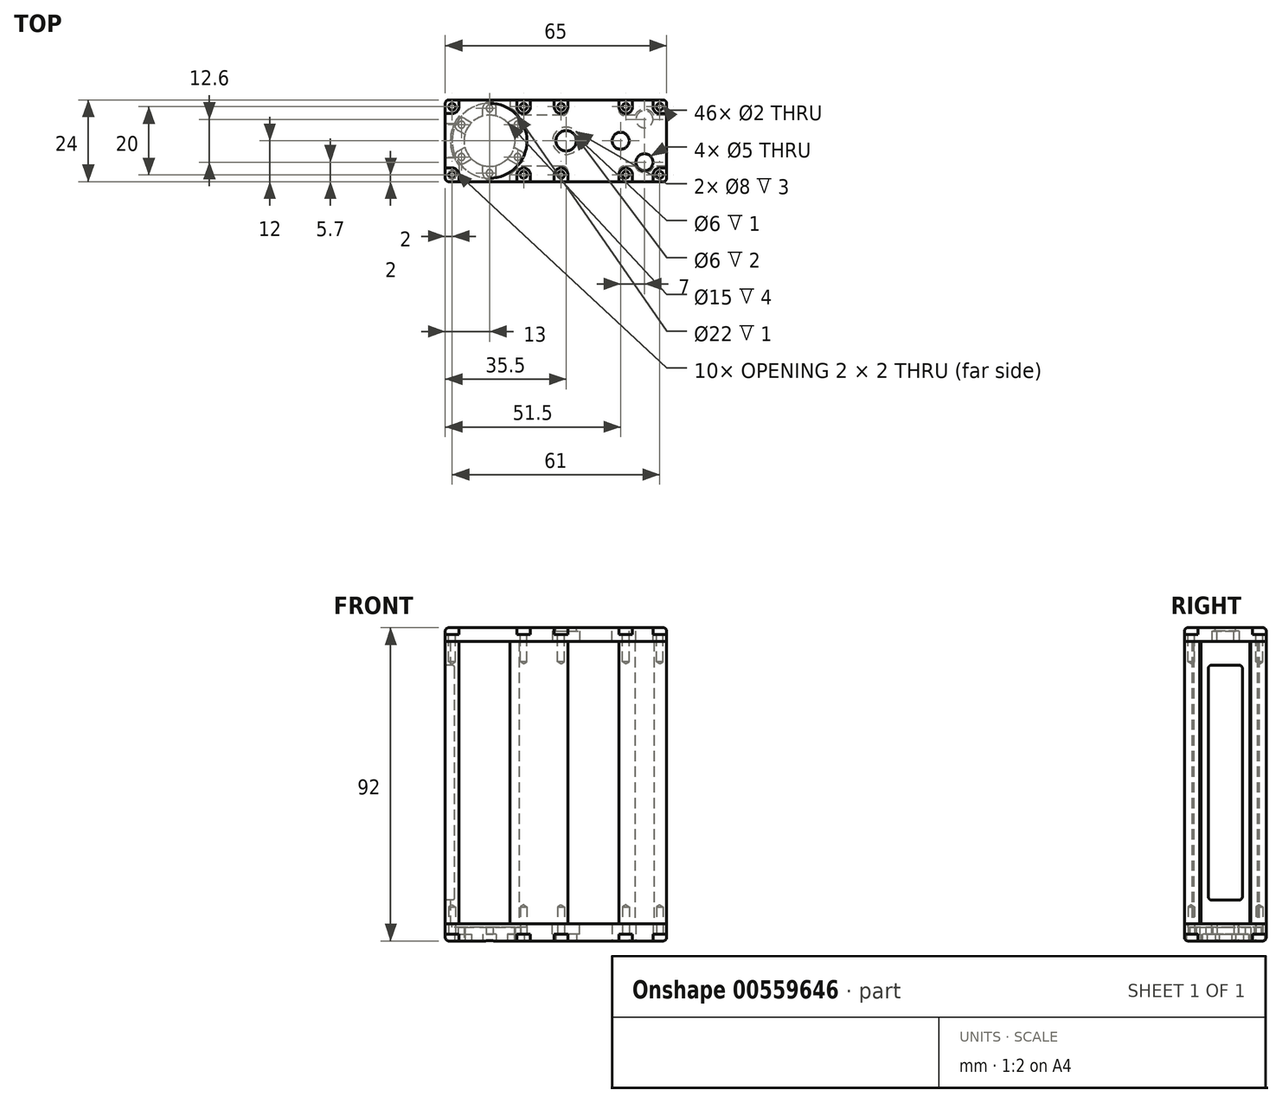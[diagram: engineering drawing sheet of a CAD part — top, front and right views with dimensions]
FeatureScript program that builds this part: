
annotation { "Feature Type Name" : "Feature", "Feature Type Description" : "" }
export const myFeature = defineFeature(function(context is Context, id is Id, definition is map)
    precondition{}
    {
        {
            var Q0;
            Q0=qCreatedBy(makeId("Top.planeOp"),FACE);
            var sketch = newSketch(context, id + "F0", { "sketchPlane" : qUnion([Q0])});
            skLineSegment(sketch, "E0.bottom", {"start": v(0, 0) * mm, "end": v(65, 0) * mm});
            skLineSegment(sketch, "E0.top", {"start": v(0, 24) * mm, "end": v(65, 24) * mm});
            skLineSegment(sketch, "E0.left", {"start": v(0, 0) * mm, "end": v(0, 24) * mm});
            skLineSegment(sketch, "E0.right", {"start": v(65, 0) * mm, "end": v(65, 24) * mm});
            skCircle(sketch, "E1", {"center": v(13, 12) * mm, "radius": 7.5 * mm});
            skCircle(sketch, "E2", {"center": v(35.5, 12) * mm, "radius": 3 * mm});
            skLineSegment(sketch, "E3", {"start": v(0, 12) * mm, "end": v(65, 12) * mm, "construction": true});
            skCircle(sketch, "E4", {"center": v(58.5, 18.3) * mm, "radius": 2.5 * mm});
            skLineSegment(sketch, "E5", {"start": v(58.5, 33.82) * mm, "end": v(58.5, -9.1) * mm, "construction": true});
            skCircle(sketch, "E6", {"center": v(51.5, 12) * mm, "radius": 2.5 * mm});
            skSolve(sketch);
        }
        {
            var Q0;
            Q0=makeQuery(id+"F0.imprint","IMPRINT",FACE,{"disambiguationData":[TD([[makeQuery(id+"F0.imprint","IMPRINT",EDGE,{"derivedFrom":sQuery(id+"F0.wireOp",EDGE,"E0.bottom")}),1.0]])]});
            extrude(context, id + "F1", {"entities" : qUnion([Q0]), "depth" : 5 * mm, "offsetDistance" : 25 * mm});
        }
        {
            var Q0;
            Q0=makeQuery(id+"F1.opExtrude","CAP_FACE",FACE,{"disambiguationData":[OSD([sQuery(id+"F0.wireOp",EDGE,"E0.bottom"),sQuery(id+"F0.wireOp",EDGE,"E0.top"),sQuery(id+"F0.wireOp",EDGE,"E0.left"),sQuery(id+"F0.wireOp",EDGE,"E0.right"),sQuery(id+"F0.wireOp",EDGE,"E1"),sQuery(id+"F0.wireOp",EDGE,"E2"),sQuery(id+"F0.wireOp",EDGE,"IlChBpbm-lz3O-i63i-vyvh-uRPtDYFZDyJ4"),sQuery(id+"F0.wireOp",EDGE,"E4"),sQuery(id+"F0.wireOp",EDGE,"DXnECD94-bbeP-FHQP-F0Iu-yloOuqhtlozA")])],"isStart":false});
            var sketch = newSketch(context, id + "F2", { "sketchPlane" : qUnion([Q0])});
            skCircle(sketch, "E7", {"center": v(13, 12) * mm, "radius": 11 * mm});
            skSolve(sketch);
        }
        {
            var Q0;
            Q0=makeQuery(id+"F2.imprint","IMPRINT",FACE,{"disambiguationData":[TD([[makeQuery(id+"F2.imprint","IMPRINT",EDGE,{"derivedFrom":makeQuery(id+"F1.opExtrude","CAP_EDGE",EDGE,{"disambiguationData":[OSD([sQuery(id+"F0.wireOp",EDGE,"E1")])],"isStart":false})}),-1.0]])]});
            extrude(context, id + "F3", {"entities" : qUnion([Q0]), "operationType" : NewBodyOperationType.REMOVE, "oppositeDirection" : true, "depth" : 1 * mm, "offsetDistance" : 25 * mm});
        }
        {
            var Q0;
            Q0=makeQuery(id+"F1.opExtrude","CAP_FACE",FACE,{"disambiguationData":[OSD([sQuery(id+"F0.wireOp",EDGE,"E0.bottom"),sQuery(id+"F0.wireOp",EDGE,"E0.top"),sQuery(id+"F0.wireOp",EDGE,"E0.left"),sQuery(id+"F0.wireOp",EDGE,"E0.right"),sQuery(id+"F0.wireOp",EDGE,"E1"),sQuery(id+"F0.wireOp",EDGE,"E2"),sQuery(id+"F0.wireOp",EDGE,"IlChBpbm-lz3O-i63i-vyvh-uRPtDYFZDyJ4"),sQuery(id+"F0.wireOp",EDGE,"E4"),sQuery(id+"F0.wireOp",EDGE,"DXnECD94-bbeP-FHQP-F0Iu-yloOuqhtlozA")])],"isStart":true});
            var sketch = newSketch(context, id + "F4", { "sketchPlane" : qUnion([Q0])});
            skCircle(sketch, "E8.cCircle", {"center": v(13, -12) * mm, "radius": 9.5 * mm, "construction": true});
            skLineSegment(sketch, "E8.0", {"start": v(13, -2.5) * mm, "end": v(21.23, -7.25) * mm});
            skLineSegment(sketch, "E8.1", {"start": v(21.23, -7.25) * mm, "end": v(21.23, -16.75) * mm});
            skLineSegment(sketch, "E8.2", {"start": v(21.23, -16.75) * mm, "end": v(13, -21.5) * mm});
            skLineSegment(sketch, "E8.3", {"start": v(13, -21.5) * mm, "end": v(4.77, -16.75) * mm});
            skLineSegment(sketch, "E8.4", {"start": v(4.77, -16.75) * mm, "end": v(4.77, -7.25) * mm});
            skLineSegment(sketch, "E8.5", {"start": v(4.77, -7.25) * mm, "end": v(13, -2.5) * mm});
            skLineSegment(sketch, "E9", {"start": v(13, -2.5) * mm, "end": v(13, -21.5) * mm, "construction": true});
            skPoint(sketch, "E10", {"position": v(13, -2.5) * mm});
            skPoint(sketch, "E11", {"position": v(4.77, -7.25) * mm});
            skPoint(sketch, "E12", {"position": v(4.77, -16.75) * mm});
            skPoint(sketch, "E13", {"position": v(13, -21.5) * mm});
            skPoint(sketch, "E14", {"position": v(21.23, -16.75) * mm});
            skPoint(sketch, "E15", {"position": v(21.23, -7.25) * mm});
            skSolve(sketch);
        }
        {
            var Q0;
            Q0=sQuery(id+"F4.wireOp",VERTEX,"E10");
            var Q1;
            Q1=sQuery(id+"F4.wireOp",VERTEX,"E11");
            var Q2;
            Q2=sQuery(id+"F4.wireOp",VERTEX,"E12");
            var Q3;
            Q3=sQuery(id+"F4.wireOp",VERTEX,"E13");
            var Q4;
            Q4=sQuery(id+"F4.wireOp",VERTEX,"E14");
            var Q5;
            Q5=sQuery(id+"F4.wireOp",VERTEX,"E15");
            var Q6;
            Q6=makeQuery(id+"F1.opExtrude","SWEPT_BODY",BODY,{"disambiguationData":[OSD([sQuery(id+"F0.wireOp",EDGE,"E0.bottom"),sQuery(id+"F0.wireOp",EDGE,"E0.top"),sQuery(id+"F0.wireOp",EDGE,"E0.left"),sQuery(id+"F0.wireOp",EDGE,"E0.right"),sQuery(id+"F0.wireOp",EDGE,"E1"),sQuery(id+"F0.wireOp",EDGE,"E2"),sQuery(id+"F0.wireOp",EDGE,"IlChBpbm-lz3O-i63i-vyvh-uRPtDYFZDyJ4"),sQuery(id+"F0.wireOp",EDGE,"E4"),sQuery(id+"F0.wireOp",EDGE,"DXnECD94-bbeP-FHQP-F0Iu-yloOuqhtlozA")])]});
            hole(context, id + "F5", {"style" : HoleStyle.SIMPLE, "endStyle" : HoleEndStyle.THROUGH, "holeDiameter" : 2 * mm, "isTappedThrough" : true, "tappedDepth" : 5 * mm, "tapClearance" : 2, "startFromSketch" : true, "locations" : qUnion([Q0, Q1, Q2, Q3, Q4, Q5]), "scope" : qUnion([Q6])});
        }
        {
            var Q0;
            Q0=makeQuery(id+"F1.opExtrude","CAP_FACE",FACE,{"disambiguationData":[OSD([sQuery(id+"F0.wireOp",EDGE,"E0.bottom"),sQuery(id+"F0.wireOp",EDGE,"E0.top"),sQuery(id+"F0.wireOp",EDGE,"E0.left"),sQuery(id+"F0.wireOp",EDGE,"E0.right"),sQuery(id+"F0.wireOp",EDGE,"E1"),sQuery(id+"F0.wireOp",EDGE,"E2"),sQuery(id+"F0.wireOp",EDGE,"IlChBpbm-lz3O-i63i-vyvh-uRPtDYFZDyJ4"),sQuery(id+"F0.wireOp",EDGE,"E4"),sQuery(id+"F0.wireOp",EDGE,"DXnECD94-bbeP-FHQP-F0Iu-yloOuqhtlozA")])],"isStart":true});
            var sketch = newSketch(context, id + "F6", { "sketchPlane" : qUnion([Q0])});
            skArc(sketch, "E16", {"start": v(15, -2.5) * mm, "mid": v(13, -0.5) * mm, "end": v(11, -2.5) * mm});
            skArc(sketch, "E17", {"start": v(5.77, -5.52) * mm, "mid": v(3.04, -6.25) * mm, "end": v(3.77, -8.98) * mm});
            skArc(sketch, "E18", {"start": v(3.77, -15.02) * mm, "mid": v(3.04, -17.75) * mm, "end": v(5.77, -18.48) * mm});
            skArc(sketch, "E19", {"start": v(11, -21.5) * mm, "mid": v(13, -23.5) * mm, "end": v(15, -21.5) * mm});
            skArc(sketch, "E20", {"start": v(22.23, -8.98) * mm, "mid": v(22.96, -6.25) * mm, "end": v(20.23, -5.52) * mm});
            skArc(sketch, "E21", {"start": v(20.23, -18.48) * mm, "mid": v(22.96, -17.75) * mm, "end": v(22.23, -15.02) * mm});
            skLineSegment(sketch, "E22", {"start": v(3.77, -8.98) * mm, "end": v(20.23, -18.48) * mm});
            skLineSegment(sketch, "E23", {"start": v(5.77, -5.52) * mm, "end": v(22.23, -15.02) * mm});
            skLineSegment(sketch, "E24", {"start": v(11, -2.5) * mm, "end": v(11, -21.5) * mm});
            skLineSegment(sketch, "E25", {"start": v(15, -2.5) * mm, "end": v(15, -21.5) * mm});
            skLineSegment(sketch, "E26", {"start": v(3.77, -15.02) * mm, "end": v(20.23, -5.52) * mm});
            skLineSegment(sketch, "E27", {"start": v(5.77, -18.48) * mm, "end": v(22.23, -8.98) * mm});
            skSolve(sketch);
        }
        {
            var Q0;
            Q0 = qSketchRegion(id + "F6", true);
            extrude(context, id + "F7", {"entities" : qUnion([Q0]), "operationType" : NewBodyOperationType.REMOVE, "oppositeDirection" : true, "depth" : 2 * mm, "offsetDistance" : 25 * mm});
        }
        {
            var Q0;
            Q0=makeQuery(id+"F1.opExtrude","CAP_FACE",FACE,{"disambiguationData":[OSD([sQuery(id+"F0.wireOp",EDGE,"E0.bottom"),sQuery(id+"F0.wireOp",EDGE,"E0.top"),sQuery(id+"F0.wireOp",EDGE,"E0.left"),sQuery(id+"F0.wireOp",EDGE,"E0.right"),sQuery(id+"F0.wireOp",EDGE,"E1"),sQuery(id+"F0.wireOp",EDGE,"E2"),sQuery(id+"F0.wireOp",EDGE,"E4"),sQuery(id+"F0.wireOp",EDGE,"DXnECD94-bbeP-FHQP-F0Iu-yloOuqhtlozA")])],"isStart":false});
            var sketch = newSketch(context, id + "F8", { "sketchPlane" : qUnion([Q0])});
            skCircle(sketch, "E28", {"center": v(35.5, 12) * mm, "radius": 4 * mm});
            skSolve(sketch);
        }
        {
            var Q0;
            Q0 = qSketchRegion(id + "F8", true);
            extrude(context, id + "F9", {"entities" : qUnion([Q0]), "operationType" : NewBodyOperationType.REMOVE, "oppositeDirection" : true, "depth" : 3 * mm, "offsetDistance" : 25 * mm});
        }
        {
            var Q0;
            Q0=qCreatedBy(makeId("Top.planeOp"),FACE);
            cPlane(context, id + "F10", {"entities" : qUnion([Q0]), "cplaneType" : CPlaneType.OFFSET, "offset" : 92 * mm, "width" : 150 * mm, "height" : 150 * mm});
        }
        {
            var Q0;
            Q0=qCreatedBy(id+"F10.planeOp",FACE);
            var sketch = newSketch(context, id + "F11", { "sketchPlane" : qUnion([Q0])});
            skLineSegment(sketch, "E29.bottom", {"start": v(0, 0) * mm, "end": v(65, 0) * mm});
            skLineSegment(sketch, "E29.top", {"start": v(0, 24) * mm, "end": v(65, 24) * mm});
            skLineSegment(sketch, "E29.left", {"start": v(0, 0) * mm, "end": v(0, 24) * mm});
            skLineSegment(sketch, "E29.right", {"start": v(65, 0) * mm, "end": v(65, 24) * mm});
            skCircle(sketch, "E30", {"center": v(51.5, 12) * mm, "radius": 2.5 * mm});
            skCircle(sketch, "E31", {"center": v(58.5, 5.7) * mm, "radius": 2.5 * mm});
            skCircle(sketch, "E32", {"center": v(35.5, 12) * mm, "radius": 3 * mm});
            skLineSegment(sketch, "E33", {"start": v(0, 12) * mm, "end": v(65, 12) * mm, "construction": true});
            skSolve(sketch);
        }
        {
            var Q0;
            Q0 = qSketchRegion(id + "F11", true);
            extrude(context, id + "F12", {"entities" : qUnion([Q0]), "oppositeDirection" : true, "depth" : 4 * mm, "offsetDistance" : 25 * mm});
        }
        {
            var Q0;
            Q0=makeQuery(id+"F12.opExtrude","CAP_FACE",FACE,{"disambiguationData":[OSD([sQuery(id+"F11.wireOp",EDGE,"E29.bottom"),sQuery(id+"F11.wireOp",EDGE,"E29.top"),sQuery(id+"F11.wireOp",EDGE,"E29.left"),sQuery(id+"F11.wireOp",EDGE,"E29.right"),sQuery(id+"F11.wireOp",EDGE,"E30"),sQuery(id+"F11.wireOp",EDGE,"E31"),sQuery(id+"F11.wireOp",EDGE,"E32")])],"isStart":false});
            var sketch = newSketch(context, id + "F13", { "sketchPlane" : qUnion([Q0])});
            skCircle(sketch, "E34", {"center": v(35.5, -12) * mm, "radius": 4 * mm});
            skSolve(sketch);
        }
        {
            var Q0;
            Q0 = qSketchRegion(id + "F13", true);
            extrude(context, id + "F14", {"entities" : qUnion([Q0]), "operationType" : NewBodyOperationType.REMOVE, "oppositeDirection" : true, "depth" : 3 * mm, "offsetDistance" : 25 * mm});
        }
        {
            var Q0;
            Q0=makeQuery(id+"F1.opExtrude","CAP_FACE",FACE,{"disambiguationData":[OSD([sQuery(id+"F0.wireOp",EDGE,"E0.bottom"),sQuery(id+"F0.wireOp",EDGE,"E0.top"),sQuery(id+"F0.wireOp",EDGE,"E0.left"),sQuery(id+"F0.wireOp",EDGE,"E0.right"),sQuery(id+"F0.wireOp",EDGE,"E1"),sQuery(id+"F0.wireOp",EDGE,"E2"),sQuery(id+"F0.wireOp",EDGE,"E4"),sQuery(id+"F0.wireOp",EDGE,"E6")])],"isStart":false});
            var sketch = newSketch(context, id + "F15", { "sketchPlane" : qUnion([Q0])});
            skLineSegment(sketch, "E35.bottom", {"start": v(0, 24) * mm, "end": v(4, 24) * mm});
            skLineSegment(sketch, "E35.top", {"start": v(0, 0) * mm, "end": v(4, 0) * mm});
            skLineSegment(sketch, "E35.left", {"start": v(0, 24) * mm, "end": v(0, 0) * mm});
            skLineSegment(sketch, "E35.right", {"start": v(4, 24) * mm, "end": v(4, 19.16) * mm});
            skArc(sketch, "E36", {"start": v(4, 19.16) * mm, "mid": v(1.5, 12) * mm, "end": v(4, 4.84) * mm});
            skLineSegment(sketch, "E37.trimOffspring", {"start": v(4, 4.84) * mm, "end": v(4, 0) * mm});
            skLineSegment(sketch, "E38", {"start": v(58.5, 18.3) * mm, "end": v(58.5, 5.7) * mm, "construction": true});
            skArc(sketch, "E39", {"start": v(61.25, 19.5) * mm, "mid": v(58.5, 21.3) * mm, "end": v(55.75, 19.5) * mm});
            skArc(sketch, "E40", {"start": v(55.75, 4.5) * mm, "mid": v(58.5, 2.7) * mm, "end": v(61.25, 4.5) * mm});
            skLineSegment(sketch, "E41.bottom", {"start": v(65, 24) * mm, "end": v(51, 24) * mm});
            skLineSegment(sketch, "E41.top", {"start": v(65, 19.5) * mm, "end": v(61.25, 19.5) * mm});
            skLineSegment(sketch, "E41.left", {"start": v(65, 24) * mm, "end": v(65, 19.5) * mm});
            skLineSegment(sketch, "E41.right", {"start": v(51, 24) * mm, "end": v(51, 21) * mm});
            skLineSegment(sketch, "E42.bottom", {"start": v(65, 0) * mm, "end": v(51, 0) * mm});
            skLineSegment(sketch, "E42.top", {"start": v(65, 4.5) * mm, "end": v(61.25, 4.5) * mm});
            skLineSegment(sketch, "E42.left", {"start": v(65, 0) * mm, "end": v(65, 4.5) * mm});
            skLineSegment(sketch, "E42.right", {"start": v(51, 0) * mm, "end": v(51, 3) * mm});
            skLineSegment(sketch, "E43.trimOffspring", {"start": v(55.75, 19.5) * mm, "end": v(52.5, 19.5) * mm});
            skLineSegment(sketch, "E44.trimOffspring", {"start": v(55.75, 4.5) * mm, "end": v(52.5, 4.5) * mm});
            skArc(sketch, "E45", {"start": v(51, 21) * mm, "mid": v(51.44, 19.94) * mm, "end": v(52.5, 19.5) * mm});
            skArc(sketch, "E46", {"start": v(52.5, 4.5) * mm, "mid": v(51.44, 4.06) * mm, "end": v(51, 3) * mm});
            skPoint(sketch, "E47.orphan", {"position": v(51, 19.5) * mm});
            skPoint(sketch, "E48.orphan", {"position": v(51, 4.5) * mm});
            skLineSegment(sketch, "E49.bottom", {"start": v(36, 24) * mm, "end": v(19, 24) * mm});
            skLineSegment(sketch, "E49.top", {"start": v(34.5, 19.5) * mm, "end": v(21.72, 19.5) * mm});
            skLineSegment(sketch, "E49.left", {"start": v(36, 24) * mm, "end": v(36, 21) * mm});
            skLineSegment(sketch, "E49.right", {"start": v(19, 24) * mm, "end": v(19, 21.81) * mm});
            skLineSegment(sketch, "E50.bottom", {"start": v(36, 0) * mm, "end": v(19, 0) * mm});
            skLineSegment(sketch, "E50.top", {"start": v(34.5, 4.5) * mm, "end": v(21.72, 4.5) * mm});
            skLineSegment(sketch, "E50.left", {"start": v(36, 0) * mm, "end": v(36, 3) * mm});
            skLineSegment(sketch, "E50.right", {"start": v(19, 0) * mm, "end": v(19, 2.19) * mm});
            skLineSegment(sketch, "E51", {"start": v(36, 19.5) * mm, "end": v(36, 4.5) * mm, "construction": true});
            skLineSegment(sketch, "E52", {"start": v(19, 19.5) * mm, "end": v(19, 4.5) * mm, "construction": true});
            skArc(sketch, "E53", {"start": v(34.5, 19.5) * mm, "mid": v(35.56, 19.94) * mm, "end": v(36, 21) * mm});
            skArc(sketch, "E54", {"start": v(36, 3) * mm, "mid": v(35.56, 4.06) * mm, "end": v(34.5, 4.5) * mm});
            skArc(sketch, "E55", {"start": v(21.72, 19.5) * mm, "mid": v(20.45, 20.76) * mm, "end": v(19, 21.81) * mm});
            skArc(sketch, "E56.trimOffspring", {"start": v(19, 2.19) * mm, "mid": v(20.45, 3.24) * mm, "end": v(21.72, 4.5) * mm});
            skSolve(sketch);
        }
        {
            var Q0;
            Q0 = qSketchRegion(id + "F15", true);
            extrude(context, id + "F16", {"entities" : qUnion([Q0]), "depth" : 83 * mm, "offsetDistance" : 25 * mm});
        }
        {
            var Q0;
            Q0=makeQuery(id+"F1.opExtrude","CAP_FACE",FACE,{"disambiguationData":[OSD([sQuery(id+"F0.wireOp",EDGE,"E0.bottom"),sQuery(id+"F0.wireOp",EDGE,"E0.top"),sQuery(id+"F0.wireOp",EDGE,"E0.left"),sQuery(id+"F0.wireOp",EDGE,"E0.right"),sQuery(id+"F0.wireOp",EDGE,"E1"),sQuery(id+"F0.wireOp",EDGE,"E2"),sQuery(id+"F0.wireOp",EDGE,"E4"),sQuery(id+"F0.wireOp",EDGE,"E6")])],"isStart":true});
            var sketch = newSketch(context, id + "F17", { "sketchPlane" : qUnion([Q0])});
            skLineSegment(sketch, "E57.bottom", {"start": v(2, -2) * mm, "end": v(63, -2) * mm, "construction": true});
            skLineSegment(sketch, "E57.top", {"start": v(2, -22) * mm, "end": v(63, -22) * mm, "construction": true});
            skLineSegment(sketch, "E57.left", {"start": v(2, -2) * mm, "end": v(2, -22) * mm, "construction": true});
            skLineSegment(sketch, "E57.right", {"start": v(63, -2) * mm, "end": v(63, -22) * mm, "construction": true});
            skPoint(sketch, "E58", {"position": v(2, -2) * mm});
            skPoint(sketch, "E59", {"position": v(2, -22) * mm});
            skPoint(sketch, "E60", {"position": v(63, -22) * mm});
            skPoint(sketch, "E61", {"position": v(63, -2) * mm});
            skLineSegment(sketch, "E62", {"start": v(53, -2) * mm, "end": v(53, -22) * mm, "construction": true});
            skLineSegment(sketch, "E63", {"start": v(34, -2) * mm, "end": v(34, -22) * mm, "construction": true});
            skLineSegment(sketch, "E64", {"start": v(23, -2) * mm, "end": v(23, -22) * mm, "construction": true});
            skPoint(sketch, "E65", {"position": v(23, -2) * mm});
            skPoint(sketch, "E66", {"position": v(34, -2) * mm});
            skPoint(sketch, "E67", {"position": v(34, -22) * mm});
            skPoint(sketch, "E68", {"position": v(23, -22) * mm});
            skPoint(sketch, "E69", {"position": v(53, -22) * mm});
            skPoint(sketch, "E70", {"position": v(53, -2) * mm});
            skSolve(sketch);
        }
        {
            var Q0;
            Q0=sQuery(id+"F17.wireOp",VERTEX,"E61");
            var Q1;
            Q1=sQuery(id+"F17.wireOp",VERTEX,"E60");
            var Q2;
            Q2=sQuery(id+"F17.wireOp",VERTEX,"E59");
            var Q3;
            Q3=sQuery(id+"F17.wireOp",VERTEX,"E58");
            var Q4;
            Q4=sQuery(id+"F17.wireOp",VERTEX,"E65");
            var Q5;
            Q5=sQuery(id+"F17.wireOp",VERTEX,"E66");
            var Q6;
            Q6=sQuery(id+"F17.wireOp",VERTEX,"E70");
            var Q7;
            Q7=sQuery(id+"F17.wireOp",VERTEX,"E69");
            var Q8;
            Q8=sQuery(id+"F17.wireOp",VERTEX,"E67");
            var Q9;
            Q9=sQuery(id+"F17.wireOp",VERTEX,"E68");
            var Q10;
            Q10=makeQuery(id+"F1.opExtrude","SWEPT_BODY",BODY,{"disambiguationData":[OSD([sQuery(id+"F0.wireOp",EDGE,"E0.bottom"),sQuery(id+"F0.wireOp",EDGE,"E0.top"),sQuery(id+"F0.wireOp",EDGE,"E0.left"),sQuery(id+"F0.wireOp",EDGE,"E0.right"),sQuery(id+"F0.wireOp",EDGE,"E1"),sQuery(id+"F0.wireOp",EDGE,"E2"),sQuery(id+"F0.wireOp",EDGE,"E4"),sQuery(id+"F0.wireOp",EDGE,"E6")])]});
            var Q11;
            Q11=makeQuery(id+"F16.opExtrude","SWEPT_BODY",BODY,{"disambiguationData":[OSD([sQuery(id+"F15.wireOp",EDGE,"sETA7IfB-NbWZ-x8hc-ehO1-osH0QOvT683d.bottom"),sQuery(id+"F15.wireOp",EDGE,"sETA7IfB-NbWZ-x8hc-ehO1-osH0QOvT683d.top"),sQuery(id+"F15.wireOp",EDGE,"sETA7IfB-NbWZ-x8hc-ehO1-osH0QOvT683d.left"),sQuery(id+"F15.wireOp",EDGE,"sETA7IfB-NbWZ-x8hc-ehO1-osH0QOvT683d.right"),sQuery(id+"F15.wireOp",EDGE,"ILhqpvC7-i7Yn-IUXK-iJsS-K77EfisCqqC3.top"),sQuery(id+"F15.wireOp",EDGE,"ILhqpvC7-i7Yn-IUXK-iJsS-K77EfisCqqC3.right"),sQuery(id+"F15.wireOp",EDGE,"2abb0f86-2ee3-4902-80a2-e3a9647c8841.trimOffspring"),sQuery(id+"F15.wireOp",EDGE,"rQa9nioj-B1Bx-91pH-sico-VFbbgBudFIM0")])]});
            var Q12;
            Q12=makeQuery(id+"F16.opExtrude","SWEPT_BODY",BODY,{"disambiguationData":[OSD([sQuery(id+"F15.wireOp",EDGE,"E35.bottom"),sQuery(id+"F15.wireOp",EDGE,"E35.top"),sQuery(id+"F15.wireOp",EDGE,"E35.left"),sQuery(id+"F15.wireOp",EDGE,"E35.right"),sQuery(id+"F15.wireOp",EDGE,"E36"),sQuery(id+"F15.wireOp",EDGE,"E37.trimOffspring")])]});
            var Q13;
            Q13=makeQuery(id+"F16.opExtrude","SWEPT_BODY",BODY,{"disambiguationData":[OSD([sQuery(id+"F15.wireOp",EDGE,"E49.bottom"),sQuery(id+"F15.wireOp",EDGE,"E49.top"),sQuery(id+"F15.wireOp",EDGE,"E49.left"),sQuery(id+"F15.wireOp",EDGE,"E49.right"),sQuery(id+"F15.wireOp",EDGE,"E53"),sQuery(id+"F15.wireOp",EDGE,"E55")])]});
            var Q14;
            Q14=makeQuery(id+"F16.opExtrude","SWEPT_BODY",BODY,{"disambiguationData":[OSD([sQuery(id+"F15.wireOp",EDGE,"E39"),sQuery(id+"F15.wireOp",EDGE,"E41.bottom"),sQuery(id+"F15.wireOp",EDGE,"E41.top"),sQuery(id+"F15.wireOp",EDGE,"E41.left"),sQuery(id+"F15.wireOp",EDGE,"E41.right"),sQuery(id+"F15.wireOp",EDGE,"E43.trimOffspring"),sQuery(id+"F15.wireOp",EDGE,"E45")])]});
            var Q15;
            Q15=makeQuery(id+"F16.opExtrude","SWEPT_BODY",BODY,{"disambiguationData":[OSD([sQuery(id+"F15.wireOp",EDGE,"E40"),sQuery(id+"F15.wireOp",EDGE,"E42.bottom"),sQuery(id+"F15.wireOp",EDGE,"E42.top"),sQuery(id+"F15.wireOp",EDGE,"E42.left"),sQuery(id+"F15.wireOp",EDGE,"E42.right"),sQuery(id+"F15.wireOp",EDGE,"E44.trimOffspring"),sQuery(id+"F15.wireOp",EDGE,"E46")])]});
            var Q16;
            Q16=makeQuery(id+"F16.opExtrude","SWEPT_BODY",BODY,{"disambiguationData":[OSD([sQuery(id+"F15.wireOp",EDGE,"E50.bottom"),sQuery(id+"F15.wireOp",EDGE,"E50.top"),sQuery(id+"F15.wireOp",EDGE,"E50.left"),sQuery(id+"F15.wireOp",EDGE,"E50.right"),sQuery(id+"F15.wireOp",EDGE,"E54"),sQuery(id+"F15.wireOp",EDGE,"E56.trimOffspring")])]});
            hole(context, id + "F18", {"style" : HoleStyle.SIMPLE, "endStyle" : HoleEndStyle.BLIND, "holeDiameter" : 2 * mm, "holeDepth" : 10 * mm, "isTappedThrough" : true, "tappedDepth" : 7 * mm, "tapClearance" : 2, "startFromSketch" : true, "locations" : qUnion([Q0, Q1, Q2, Q3, Q4, Q5, Q6, Q7, Q8, Q9]), "scope" : qUnion([Q10, Q11, Q12, Q13, Q14, Q15, Q16])});
        }
        {
            var Q0;
            Q0=makeQuery(id+"F1.opExtrude","CAP_FACE",FACE,{"disambiguationData":[OSD([sQuery(id+"F0.wireOp",EDGE,"E0.bottom"),sQuery(id+"F0.wireOp",EDGE,"E0.top"),sQuery(id+"F0.wireOp",EDGE,"E0.left"),sQuery(id+"F0.wireOp",EDGE,"E0.right"),sQuery(id+"F0.wireOp",EDGE,"E1"),sQuery(id+"F0.wireOp",EDGE,"E2"),sQuery(id+"F0.wireOp",EDGE,"E4"),sQuery(id+"F0.wireOp",EDGE,"E6")])],"isStart":true});
            var sketch = newSketch(context, id + "F19", { "sketchPlane" : qUnion([Q0])});
            skArc(sketch, "E71", {"start": v(61, -2) * mm, "mid": v(61.59, -3.41) * mm, "end": v(63, -4) * mm});
            skArc(sketch, "E72", {"start": v(63, -20) * mm, "mid": v(61.59, -20.59) * mm, "end": v(61, -22) * mm});
            skArc(sketch, "E73", {"start": v(2, -4) * mm, "mid": v(3.41, -3.41) * mm, "end": v(4, -2) * mm});
            skArc(sketch, "E74", {"start": v(4, -22) * mm, "mid": v(3.41, -20.59) * mm, "end": v(2, -20) * mm});
            skLineSegment(sketch, "E75", {"start": v(4, -2) * mm, "end": v(4, 0) * mm});
            skLineSegment(sketch, "E76", {"start": v(4, 0) * mm, "end": v(0, 0) * mm});
            skLineSegment(sketch, "E77", {"start": v(0, 0) * mm, "end": v(0, -4) * mm});
            skLineSegment(sketch, "E78", {"start": v(0, -4) * mm, "end": v(2, -4) * mm});
            skLineSegment(sketch, "E79", {"start": v(4, -22) * mm, "end": v(4, -24) * mm});
            skLineSegment(sketch, "E80", {"start": v(4, -24) * mm, "end": v(0, -24) * mm});
            skLineSegment(sketch, "E81", {"start": v(0, -24) * mm, "end": v(0, -20) * mm});
            skLineSegment(sketch, "E82", {"start": v(0, -20) * mm, "end": v(2, -20) * mm});
            skLineSegment(sketch, "E83", {"start": v(61, -2) * mm, "end": v(61, 0) * mm});
            skLineSegment(sketch, "E84", {"start": v(61, 0) * mm, "end": v(65, 0) * mm});
            skLineSegment(sketch, "E85", {"start": v(65, 0) * mm, "end": v(65, -4) * mm});
            skLineSegment(sketch, "E86", {"start": v(65, -4) * mm, "end": v(63, -4) * mm});
            skLineSegment(sketch, "E87", {"start": v(63, -20) * mm, "end": v(65, -20) * mm});
            skLineSegment(sketch, "E88", {"start": v(65, -20) * mm, "end": v(65, -24) * mm});
            skLineSegment(sketch, "E89", {"start": v(65, -24) * mm, "end": v(61, -24) * mm});
            skLineSegment(sketch, "E90", {"start": v(61, -24) * mm, "end": v(61, -22) * mm});
            skArc(sketch, "E91", {"start": v(21, -2) * mm, "mid": v(23, -4) * mm, "end": v(25, -2) * mm});
            skArc(sketch, "E92", {"start": v(32, -2) * mm, "mid": v(34, -4) * mm, "end": v(36, -2) * mm});
            skArc(sketch, "E93", {"start": v(51, -2) * mm, "mid": v(53, -4) * mm, "end": v(55, -2) * mm});
            skArc(sketch, "E94", {"start": v(55, -22) * mm, "mid": v(53, -20) * mm, "end": v(51, -22) * mm});
            skArc(sketch, "E95", {"start": v(36, -22) * mm, "mid": v(34, -20) * mm, "end": v(32, -22) * mm});
            skArc(sketch, "E96", {"start": v(25, -22) * mm, "mid": v(23, -20) * mm, "end": v(21, -22) * mm});
            skLineSegment(sketch, "E97", {"start": v(21, -2) * mm, "end": v(21, 0) * mm});
            skLineSegment(sketch, "E98", {"start": v(21, 0) * mm, "end": v(25, 0) * mm});
            skLineSegment(sketch, "E99", {"start": v(25, 0) * mm, "end": v(25, -2) * mm});
            skLineSegment(sketch, "E100", {"start": v(32, -2) * mm, "end": v(32, 0) * mm});
            skLineSegment(sketch, "E101", {"start": v(32, 0) * mm, "end": v(36, 0) * mm});
            skLineSegment(sketch, "E102", {"start": v(36, 0) * mm, "end": v(36, -2) * mm});
            skLineSegment(sketch, "E103", {"start": v(51, -2) * mm, "end": v(51, 0) * mm});
            skLineSegment(sketch, "E104", {"start": v(51, 0) * mm, "end": v(55, 0) * mm});
            skLineSegment(sketch, "E105", {"start": v(55, 0) * mm, "end": v(55, -2) * mm});
            skLineSegment(sketch, "E106", {"start": v(21, -22) * mm, "end": v(21, -24) * mm});
            skLineSegment(sketch, "E107", {"start": v(21, -24) * mm, "end": v(25, -24) * mm});
            skLineSegment(sketch, "E108", {"start": v(25, -24) * mm, "end": v(25, -22) * mm});
            skLineSegment(sketch, "E109", {"start": v(32, -22) * mm, "end": v(32, -24) * mm});
            skLineSegment(sketch, "E110", {"start": v(32, -24) * mm, "end": v(36, -24) * mm});
            skLineSegment(sketch, "E111", {"start": v(36, -24) * mm, "end": v(36, -22) * mm});
            skLineSegment(sketch, "E112", {"start": v(51, -22) * mm, "end": v(51, -24) * mm});
            skLineSegment(sketch, "E113", {"start": v(51, -24) * mm, "end": v(55, -24) * mm});
            skLineSegment(sketch, "E114", {"start": v(55, -24) * mm, "end": v(55, -22) * mm});
            skSolve(sketch);
        }
        {
            var Q0;
            Q0 = qSketchRegion(id + "F19", true);
            extrude(context, id + "F20", {"entities" : qUnion([Q0]), "operationType" : NewBodyOperationType.REMOVE, "oppositeDirection" : true, "depth" : 2 * mm, "offsetDistance" : 25 * mm});
        }
        {
            var Q0;
            Q0=makeQuery(id+"F12.opExtrude","CAP_FACE",FACE,{"disambiguationData":[OSD([sQuery(id+"F11.wireOp",EDGE,"E29.bottom"),sQuery(id+"F11.wireOp",EDGE,"E29.top"),sQuery(id+"F11.wireOp",EDGE,"E29.left"),sQuery(id+"F11.wireOp",EDGE,"E29.right"),sQuery(id+"F11.wireOp",EDGE,"E30"),sQuery(id+"F11.wireOp",EDGE,"E31"),sQuery(id+"F11.wireOp",EDGE,"E32")])],"isStart":true});
            var sketch = newSketch(context, id + "F21", { "sketchPlane" : qUnion([Q0])});
            skLineSegment(sketch, "E115.bottom", {"start": v(2, 22) * mm, "end": v(63, 22) * mm, "construction": true});
            skLineSegment(sketch, "E115.top", {"start": v(2, 2) * mm, "end": v(63, 2) * mm, "construction": true});
            skLineSegment(sketch, "E115.left", {"start": v(2, 22) * mm, "end": v(2, 2) * mm, "construction": true});
            skLineSegment(sketch, "E115.right", {"start": v(63, 22) * mm, "end": v(63, 2) * mm, "construction": true});
            skPoint(sketch, "E116", {"position": v(2, 22) * mm});
            skPoint(sketch, "E117", {"position": v(2, 2) * mm});
            skPoint(sketch, "E118", {"position": v(63, 2) * mm});
            skPoint(sketch, "E119", {"position": v(63, 22) * mm});
            skLineSegment(sketch, "E120", {"start": v(53, 2) * mm, "end": v(53, 22) * mm, "construction": true});
            skLineSegment(sketch, "E121", {"start": v(34, 2) * mm, "end": v(34, 22) * mm, "construction": true});
            skLineSegment(sketch, "E122", {"start": v(23, 22) * mm, "end": v(23, 2) * mm, "construction": true});
            skPoint(sketch, "E123", {"position": v(23, 22) * mm});
            skPoint(sketch, "E124", {"position": v(34, 22) * mm});
            skPoint(sketch, "E125", {"position": v(53, 2) * mm});
            skPoint(sketch, "E126", {"position": v(53, 22) * mm});
            skPoint(sketch, "E127", {"position": v(34, 2) * mm});
            skPoint(sketch, "E128", {"position": v(23, 2) * mm});
            skSolve(sketch);
        }
        {
            var Q0;
            Q0=sQuery(id+"F21.wireOp",VERTEX,"E116");
            var Q1;
            Q1=sQuery(id+"F21.wireOp",VERTEX,"E117");
            var Q2;
            Q2=sQuery(id+"F21.wireOp",VERTEX,"E118");
            var Q3;
            Q3=sQuery(id+"F21.wireOp",VERTEX,"E119");
            var Q4;
            Q4=sQuery(id+"F21.wireOp",VERTEX,"E126");
            var Q5;
            Q5=sQuery(id+"F21.wireOp",VERTEX,"E125");
            var Q6;
            Q6=sQuery(id+"F21.wireOp",VERTEX,"E127");
            var Q7;
            Q7=sQuery(id+"F21.wireOp",VERTEX,"E128");
            var Q8;
            Q8=sQuery(id+"F21.wireOp",VERTEX,"E123");
            var Q9;
            Q9=sQuery(id+"F21.wireOp",VERTEX,"E124");
            var Q10;
            Q10=makeQuery(id+"F12.opExtrude","SWEPT_BODY",BODY,{"disambiguationData":[OSD([sQuery(id+"F11.wireOp",EDGE,"E29.bottom"),sQuery(id+"F11.wireOp",EDGE,"E29.top"),sQuery(id+"F11.wireOp",EDGE,"E29.left"),sQuery(id+"F11.wireOp",EDGE,"E29.right"),sQuery(id+"F11.wireOp",EDGE,"E30"),sQuery(id+"F11.wireOp",EDGE,"E31"),sQuery(id+"F11.wireOp",EDGE,"E32")])]});
            var Q11;
            Q11=makeQuery(id+"F16.opExtrude","SWEPT_BODY",BODY,{"disambiguationData":[OSD([sQuery(id+"F15.wireOp",EDGE,"E35.bottom"),sQuery(id+"F15.wireOp",EDGE,"E35.top"),sQuery(id+"F15.wireOp",EDGE,"E35.left"),sQuery(id+"F15.wireOp",EDGE,"E35.right"),sQuery(id+"F15.wireOp",EDGE,"E36"),sQuery(id+"F15.wireOp",EDGE,"E37.trimOffspring")])]});
            var Q12;
            Q12=makeQuery(id+"F16.opExtrude","SWEPT_BODY",BODY,{"disambiguationData":[OSD([sQuery(id+"F15.wireOp",EDGE,"sETA7IfB-NbWZ-x8hc-ehO1-osH0QOvT683d.bottom"),sQuery(id+"F15.wireOp",EDGE,"sETA7IfB-NbWZ-x8hc-ehO1-osH0QOvT683d.top"),sQuery(id+"F15.wireOp",EDGE,"sETA7IfB-NbWZ-x8hc-ehO1-osH0QOvT683d.left"),sQuery(id+"F15.wireOp",EDGE,"sETA7IfB-NbWZ-x8hc-ehO1-osH0QOvT683d.right"),sQuery(id+"F15.wireOp",EDGE,"ILhqpvC7-i7Yn-IUXK-iJsS-K77EfisCqqC3.top"),sQuery(id+"F15.wireOp",EDGE,"ILhqpvC7-i7Yn-IUXK-iJsS-K77EfisCqqC3.right"),sQuery(id+"F15.wireOp",EDGE,"2abb0f86-2ee3-4902-80a2-e3a9647c8841.trimOffspring"),sQuery(id+"F15.wireOp",EDGE,"rQa9nioj-B1Bx-91pH-sico-VFbbgBudFIM0")])]});
            var Q13;
            Q13=makeQuery(id+"F16.opExtrude","SWEPT_BODY",BODY,{"disambiguationData":[OSD([sQuery(id+"F15.wireOp",EDGE,"E50.bottom"),sQuery(id+"F15.wireOp",EDGE,"E50.top"),sQuery(id+"F15.wireOp",EDGE,"E50.left"),sQuery(id+"F15.wireOp",EDGE,"E50.right"),sQuery(id+"F15.wireOp",EDGE,"E54"),sQuery(id+"F15.wireOp",EDGE,"E56.trimOffspring")])]});
            var Q14;
            Q14=makeQuery(id+"F16.opExtrude","SWEPT_BODY",BODY,{"disambiguationData":[OSD([sQuery(id+"F15.wireOp",EDGE,"E40"),sQuery(id+"F15.wireOp",EDGE,"E42.bottom"),sQuery(id+"F15.wireOp",EDGE,"E42.top"),sQuery(id+"F15.wireOp",EDGE,"E42.left"),sQuery(id+"F15.wireOp",EDGE,"E42.right"),sQuery(id+"F15.wireOp",EDGE,"E44.trimOffspring"),sQuery(id+"F15.wireOp",EDGE,"E46")])]});
            var Q15;
            Q15=makeQuery(id+"F16.opExtrude","SWEPT_BODY",BODY,{"disambiguationData":[OSD([sQuery(id+"F15.wireOp",EDGE,"E39"),sQuery(id+"F15.wireOp",EDGE,"E41.bottom"),sQuery(id+"F15.wireOp",EDGE,"E41.top"),sQuery(id+"F15.wireOp",EDGE,"E41.left"),sQuery(id+"F15.wireOp",EDGE,"E41.right"),sQuery(id+"F15.wireOp",EDGE,"E43.trimOffspring"),sQuery(id+"F15.wireOp",EDGE,"E45")])]});
            var Q16;
            Q16=makeQuery(id+"F16.opExtrude","SWEPT_BODY",BODY,{"disambiguationData":[OSD([sQuery(id+"F15.wireOp",EDGE,"E49.bottom"),sQuery(id+"F15.wireOp",EDGE,"E49.top"),sQuery(id+"F15.wireOp",EDGE,"E49.left"),sQuery(id+"F15.wireOp",EDGE,"E49.right"),sQuery(id+"F15.wireOp",EDGE,"E53"),sQuery(id+"F15.wireOp",EDGE,"E55")])]});
            hole(context, id + "F22", {"style" : HoleStyle.SIMPLE, "endStyle" : HoleEndStyle.BLIND, "holeDiameter" : 2 * mm, "holeDepth" : 10 * mm, "isTappedThrough" : true, "tappedDepth" : 7 * mm, "tapClearance" : 2, "startFromSketch" : true, "locations" : qUnion([Q0, Q1, Q2, Q3, Q4, Q5, Q6, Q7, Q8, Q9]), "scope" : qUnion([Q10, Q11, Q12, Q13, Q14, Q15, Q16])});
        }
        {
            var Q0;
            Q0=makeQuery(id+"F12.opExtrude","CAP_FACE",FACE,{"disambiguationData":[OSD([sQuery(id+"F11.wireOp",EDGE,"E29.bottom"),sQuery(id+"F11.wireOp",EDGE,"E29.top"),sQuery(id+"F11.wireOp",EDGE,"E29.left"),sQuery(id+"F11.wireOp",EDGE,"E29.right"),sQuery(id+"F11.wireOp",EDGE,"E30"),sQuery(id+"F11.wireOp",EDGE,"E31"),sQuery(id+"F11.wireOp",EDGE,"E32")])],"isStart":true});
            var sketch = newSketch(context, id + "F23", { "sketchPlane" : qUnion([Q0])});
            skArc(sketch, "E129", {"start": v(2, 20) * mm, "mid": v(3.41, 20.59) * mm, "end": v(4, 22) * mm});
            skArc(sketch, "E130", {"start": v(4, 2) * mm, "mid": v(3.41, 3.41) * mm, "end": v(2, 4) * mm});
            skArc(sketch, "E131", {"start": v(63, 4) * mm, "mid": v(61.59, 3.41) * mm, "end": v(61, 2) * mm});
            skArc(sketch, "E132", {"start": v(61, 22) * mm, "mid": v(61.59, 20.59) * mm, "end": v(63, 20) * mm});
            skLineSegment(sketch, "E133", {"start": v(4, 22) * mm, "end": v(4, 24) * mm});
            skLineSegment(sketch, "E134", {"start": v(4, 24) * mm, "end": v(0, 24) * mm});
            skLineSegment(sketch, "E135", {"start": v(0, 24) * mm, "end": v(0, 20) * mm});
            skLineSegment(sketch, "E136", {"start": v(0, 20) * mm, "end": v(2, 20) * mm});
            skLineSegment(sketch, "E137", {"start": v(2, 4) * mm, "end": v(0, 4) * mm});
            skLineSegment(sketch, "E138", {"start": v(0, 4) * mm, "end": v(0, 0) * mm});
            skLineSegment(sketch, "E139", {"start": v(0, 0) * mm, "end": v(4, 0) * mm});
            skLineSegment(sketch, "E140", {"start": v(4, 0) * mm, "end": v(4, 2) * mm});
            skLineSegment(sketch, "E141", {"start": v(61, 22) * mm, "end": v(61, 24) * mm});
            skLineSegment(sketch, "E142", {"start": v(61, 24) * mm, "end": v(65, 24) * mm});
            skLineSegment(sketch, "E143", {"start": v(65, 24) * mm, "end": v(65, 20) * mm});
            skLineSegment(sketch, "E144", {"start": v(65, 20) * mm, "end": v(63, 20) * mm});
            skLineSegment(sketch, "E145", {"start": v(63, 4) * mm, "end": v(65, 4) * mm});
            skLineSegment(sketch, "E146", {"start": v(65, 4) * mm, "end": v(65, 0) * mm});
            skLineSegment(sketch, "E147", {"start": v(65, 0) * mm, "end": v(61, 0) * mm});
            skLineSegment(sketch, "E148", {"start": v(61, 0) * mm, "end": v(61, 2) * mm});
            skArc(sketch, "E149", {"start": v(21, 22) * mm, "mid": v(23, 20) * mm, "end": v(25, 22) * mm});
            skArc(sketch, "E150", {"start": v(25, 2) * mm, "mid": v(23, 4) * mm, "end": v(21, 2) * mm});
            skLineSegment(sketch, "E151", {"start": v(21, 22) * mm, "end": v(21, 24) * mm});
            skLineSegment(sketch, "E152", {"start": v(21, 24) * mm, "end": v(25, 24) * mm});
            skLineSegment(sketch, "E153", {"start": v(25, 24) * mm, "end": v(25, 22) * mm});
            skLineSegment(sketch, "E154", {"start": v(21, 2) * mm, "end": v(21, 0) * mm});
            skLineSegment(sketch, "E155", {"start": v(21, 0) * mm, "end": v(25, 0) * mm});
            skLineSegment(sketch, "E156", {"start": v(25, 0) * mm, "end": v(25, 2) * mm});
            skArc(sketch, "E157", {"start": v(32, 22) * mm, "mid": v(34, 20) * mm, "end": v(36, 22) * mm});
            skArc(sketch, "E158", {"start": v(51, 22) * mm, "mid": v(53, 20) * mm, "end": v(55, 22) * mm});
            skArc(sketch, "E159", {"start": v(55, 2) * mm, "mid": v(53, 4) * mm, "end": v(51, 2) * mm});
            skArc(sketch, "E160", {"start": v(36, 2) * mm, "mid": v(34, 4) * mm, "end": v(32, 2) * mm});
            skLineSegment(sketch, "E161", {"start": v(32, 22) * mm, "end": v(32, 24) * mm});
            skLineSegment(sketch, "E162", {"start": v(32, 24) * mm, "end": v(36, 24) * mm});
            skLineSegment(sketch, "E163", {"start": v(36, 24) * mm, "end": v(36, 22) * mm});
            skLineSegment(sketch, "E164", {"start": v(51, 22) * mm, "end": v(51, 24) * mm});
            skLineSegment(sketch, "E165", {"start": v(51, 24) * mm, "end": v(55, 24) * mm});
            skLineSegment(sketch, "E166", {"start": v(55, 24) * mm, "end": v(55, 22) * mm});
            skLineSegment(sketch, "E167", {"start": v(32, 2) * mm, "end": v(32, 0) * mm});
            skLineSegment(sketch, "E168", {"start": v(32, 0) * mm, "end": v(36, 0) * mm});
            skLineSegment(sketch, "E169", {"start": v(36, 0) * mm, "end": v(36, 2) * mm});
            skLineSegment(sketch, "E170", {"start": v(51, 2) * mm, "end": v(51, 0) * mm});
            skLineSegment(sketch, "E171", {"start": v(51, 0) * mm, "end": v(55, 0) * mm});
            skLineSegment(sketch, "E172", {"start": v(55, 0) * mm, "end": v(55, 2) * mm});
            skSolve(sketch);
        }
        {
            var Q0;
            Q0 = qSketchRegion(id + "F23", true);
            extrude(context, id + "F24", {"entities" : qUnion([Q0]), "operationType" : NewBodyOperationType.REMOVE, "oppositeDirection" : true, "depth" : 2 * mm, "offsetDistance" : 25 * mm});
        }
        {
            var Q0;
            Q0=makeQuery(id+"F16.opExtrude","SWEPT_FACE",FACE,{"disambiguationData":[OSD([sQuery(id+"F15.wireOp",EDGE,"E35.left")])]});
            var sketch = newSketch(context, id + "F25", { "sketchPlane" : qUnion([Q0])});
            skLineSegment(sketch, "E173.bottom", {"start": v(-17, 81) * mm, "end": v(-7, 81) * mm});
            skLineSegment(sketch, "E173.top", {"start": v(-17, 12) * mm, "end": v(-7, 12) * mm});
            skLineSegment(sketch, "E173.left", {"start": v(-17, 81) * mm, "end": v(-17, 12) * mm});
            skLineSegment(sketch, "E173.right", {"start": v(-7, 81) * mm, "end": v(-7, 12) * mm});
            skSolve(sketch);
        }
        {
            var Q0;
            Q0 = qSketchRegion(id + "F25", true);
            extrude(context, id + "F26", {"entities" : qUnion([Q0]), "operationType" : NewBodyOperationType.REMOVE, "endBound" : BoundingType.THROUGH_ALL, "oppositeDirection" : true, "depth" : 25 * mm, "offsetDistance" : 25 * mm});
        }
        {
            var Q0;
            {var subQ0=sQuery(id+"F11.wireOp",EDGE,"E29.bottom");Q0=makeQuery(id+"F24.boolean.opBoolean","SPLIT",EDGE,{"disambiguationData":[TD([makeQuery(id+"F24.opExtrude","SWEPT_FACE",FACE,{"disambiguationData":[OSD([sQuery(id+"F23.wireOp",EDGE,"E140")])]})])],"derivedFrom":makeQuery(id+"F12.opExtrude","CAP_EDGE",EDGE,{"disambiguationData":[OSD([subQ0])],"isStart":true})});}
            var Q1;
            {var subQ0=sQuery(id+"F11.wireOp",EDGE,"E29.bottom");Q1=makeQuery(id+"F24.boolean.opBoolean","SPLIT",EDGE,{"disambiguationData":[TD([makeQuery(id+"F24.opExtrude","SWEPT_FACE",FACE,{"disambiguationData":[OSD([sQuery(id+"F23.wireOp",EDGE,"E156")])]})])],"derivedFrom":makeQuery(id+"F12.opExtrude","CAP_EDGE",EDGE,{"disambiguationData":[OSD([subQ0])],"isStart":true})});}
            var Q2;
            {var subQ0=sQuery(id+"F11.wireOp",EDGE,"E29.bottom");Q2=makeQuery(id+"F24.boolean.opBoolean","SPLIT",EDGE,{"disambiguationData":[TD([makeQuery(id+"F24.opExtrude","SWEPT_FACE",FACE,{"disambiguationData":[OSD([sQuery(id+"F23.wireOp",EDGE,"E169")])]})])],"derivedFrom":makeQuery(id+"F12.opExtrude","CAP_EDGE",EDGE,{"disambiguationData":[OSD([subQ0])],"isStart":true})});}
            var Q3;
            {var subQ0=sQuery(id+"F11.wireOp",EDGE,"E29.bottom");Q3=makeQuery(id+"F24.boolean.opBoolean","SPLIT",EDGE,{"disambiguationData":[TD([makeQuery(id+"F24.opExtrude","SWEPT_FACE",FACE,{"disambiguationData":[OSD([sQuery(id+"F23.wireOp",EDGE,"E148")])]})])],"derivedFrom":makeQuery(id+"F12.opExtrude","CAP_EDGE",EDGE,{"disambiguationData":[OSD([subQ0])],"isStart":true})});}
            var Q4;
            Q4=makeQuery(id+"F12.opExtrude","CAP_EDGE",EDGE,{"disambiguationData":[OSD([sQuery(id+"F11.wireOp",EDGE,"E29.right")])],"isStart":true});
            var Q5;
            {var subQ0=sQuery(id+"F11.wireOp",EDGE,"E29.top");Q5=makeQuery(id+"F24.boolean.opBoolean","SPLIT",EDGE,{"disambiguationData":[TD([makeQuery(id+"F24.opExtrude","SWEPT_FACE",FACE,{"disambiguationData":[OSD([sQuery(id+"F23.wireOp",EDGE,"E141")])]})])],"derivedFrom":makeQuery(id+"F12.opExtrude","CAP_EDGE",EDGE,{"disambiguationData":[OSD([subQ0])],"isStart":true})});}
            var Q6;
            {var subQ0=sQuery(id+"F11.wireOp",EDGE,"E29.top");Q6=makeQuery(id+"F24.boolean.opBoolean","SPLIT",EDGE,{"disambiguationData":[TD([makeQuery(id+"F24.opExtrude","SWEPT_FACE",FACE,{"disambiguationData":[OSD([sQuery(id+"F23.wireOp",EDGE,"E163")])]})])],"derivedFrom":makeQuery(id+"F12.opExtrude","CAP_EDGE",EDGE,{"disambiguationData":[OSD([subQ0])],"isStart":true})});}
            var Q7;
            {var subQ0=sQuery(id+"F11.wireOp",EDGE,"E29.top");Q7=makeQuery(id+"F24.boolean.opBoolean","SPLIT",EDGE,{"disambiguationData":[TD([makeQuery(id+"F24.opExtrude","SWEPT_FACE",FACE,{"disambiguationData":[OSD([sQuery(id+"F23.wireOp",EDGE,"E153")])]})])],"derivedFrom":makeQuery(id+"F12.opExtrude","CAP_EDGE",EDGE,{"disambiguationData":[OSD([subQ0])],"isStart":true})});}
            var Q8;
            {var subQ0=sQuery(id+"F11.wireOp",EDGE,"E29.top");Q8=makeQuery(id+"F24.boolean.opBoolean","SPLIT",EDGE,{"disambiguationData":[TD([makeQuery(id+"F24.opExtrude","SWEPT_FACE",FACE,{"disambiguationData":[OSD([sQuery(id+"F23.wireOp",EDGE,"E133")])]})])],"derivedFrom":makeQuery(id+"F12.opExtrude","CAP_EDGE",EDGE,{"disambiguationData":[OSD([subQ0])],"isStart":true})});}
            var Q9;
            Q9=makeQuery(id+"F12.opExtrude","CAP_EDGE",EDGE,{"disambiguationData":[OSD([sQuery(id+"F11.wireOp",EDGE,"E29.left")])],"isStart":true});
            var Q10;
            Q10=makeQuery(id+"F16.opExtrude","SWEPT_EDGE",EDGE,{"disambiguationData":[OSD([sQuery(id+"F15.wireOp",EDGE,"E42.bottom"),sQuery(id+"F15.wireOp",EDGE,"E42.left")])]});
            var Q11;
            Q11=makeQuery(id+"F16.opExtrude","SWEPT_EDGE",EDGE,{"disambiguationData":[OSD([sQuery(id+"F15.wireOp",EDGE,"E35.top"),sQuery(id+"F15.wireOp",EDGE,"E35.left")])]});
            var Q12;
            Q12=makeQuery(id+"F12.opExtrude","SWEPT_EDGE",EDGE,{"disambiguationData":[OSD([sQuery(id+"F11.wireOp",EDGE,"E29.bottom"),sQuery(id+"F11.wireOp",EDGE,"E29.left")])]});
            var Q13;
            Q13=makeQuery(id+"F12.opExtrude","SWEPT_EDGE",EDGE,{"disambiguationData":[OSD([sQuery(id+"F11.wireOp",EDGE,"E29.bottom"),sQuery(id+"F11.wireOp",EDGE,"E29.right")])]});
            var Q14;
            Q14=makeQuery(id+"F12.opExtrude","SWEPT_EDGE",EDGE,{"disambiguationData":[OSD([sQuery(id+"F11.wireOp",EDGE,"E29.top"),sQuery(id+"F11.wireOp",EDGE,"E29.right")])]});
            var Q15;
            Q15=makeQuery(id+"F16.opExtrude","SWEPT_EDGE",EDGE,{"disambiguationData":[OSD([sQuery(id+"F15.wireOp",EDGE,"E41.bottom"),sQuery(id+"F15.wireOp",EDGE,"E41.left")])]});
            var Q16;
            Q16=makeQuery(id+"F12.opExtrude","SWEPT_EDGE",EDGE,{"disambiguationData":[OSD([sQuery(id+"F11.wireOp",EDGE,"E29.top"),sQuery(id+"F11.wireOp",EDGE,"E29.left")])]});
            var Q17;
            Q17=makeQuery(id+"F16.opExtrude","SWEPT_EDGE",EDGE,{"disambiguationData":[OSD([sQuery(id+"F15.wireOp",EDGE,"E35.bottom"),sQuery(id+"F15.wireOp",EDGE,"E35.left")])]});
            var Q18;
            {var subQ0=sQuery(id+"F0.wireOp",EDGE,"E0.bottom");Q18=makeQuery(id+"F20.boolean.opBoolean","SPLIT",EDGE,{"disambiguationData":[TD([makeQuery(id+"F20.opExtrude","SWEPT_FACE",FACE,{"disambiguationData":[OSD([sQuery(id+"F19.wireOp",EDGE,"E75")])]})])],"derivedFrom":makeQuery(id+"F1.opExtrude","CAP_EDGE",EDGE,{"disambiguationData":[OSD([subQ0])],"isStart":true})});}
            var Q19;
            Q19=makeQuery(id+"F1.opExtrude","SWEPT_EDGE",EDGE,{"disambiguationData":[OSD([sQuery(id+"F0.wireOp",EDGE,"E0.bottom"),sQuery(id+"F0.wireOp",EDGE,"E0.left")])]});
            var Q20;
            {var subQ0=sQuery(id+"F0.wireOp",EDGE,"E0.bottom");Q20=makeQuery(id+"F20.boolean.opBoolean","SPLIT",EDGE,{"disambiguationData":[TD([makeQuery(id+"F20.opExtrude","SWEPT_FACE",FACE,{"disambiguationData":[OSD([sQuery(id+"F19.wireOp",EDGE,"E99")])]})])],"derivedFrom":makeQuery(id+"F1.opExtrude","CAP_EDGE",EDGE,{"disambiguationData":[OSD([subQ0])],"isStart":true})});}
            var Q21;
            {var subQ0=sQuery(id+"F0.wireOp",EDGE,"E0.bottom");Q21=makeQuery(id+"F20.boolean.opBoolean","SPLIT",EDGE,{"disambiguationData":[TD([makeQuery(id+"F20.opExtrude","SWEPT_FACE",FACE,{"disambiguationData":[OSD([sQuery(id+"F19.wireOp",EDGE,"E102")])]})])],"derivedFrom":makeQuery(id+"F1.opExtrude","CAP_EDGE",EDGE,{"disambiguationData":[OSD([subQ0])],"isStart":true})});}
            var Q22;
            {var subQ0=sQuery(id+"F0.wireOp",EDGE,"E0.bottom");Q22=makeQuery(id+"F20.boolean.opBoolean","SPLIT",EDGE,{"disambiguationData":[TD([makeQuery(id+"F20.opExtrude","SWEPT_FACE",FACE,{"disambiguationData":[OSD([sQuery(id+"F19.wireOp",EDGE,"E83")])]})])],"derivedFrom":makeQuery(id+"F1.opExtrude","CAP_EDGE",EDGE,{"disambiguationData":[OSD([subQ0])],"isStart":true})});}
            var Q23;
            Q23=makeQuery(id+"F1.opExtrude","CAP_EDGE",EDGE,{"disambiguationData":[OSD([sQuery(id+"F0.wireOp",EDGE,"E0.right")])],"isStart":true});
            var Q24;
            Q24=makeQuery(id+"F1.opExtrude","SWEPT_EDGE",EDGE,{"disambiguationData":[OSD([sQuery(id+"F0.wireOp",EDGE,"E0.bottom"),sQuery(id+"F0.wireOp",EDGE,"E0.right")])]});
            var Q25;
            Q25=makeQuery(id+"F1.opExtrude","SWEPT_EDGE",EDGE,{"disambiguationData":[OSD([sQuery(id+"F0.wireOp",EDGE,"E0.top"),sQuery(id+"F0.wireOp",EDGE,"E0.right")])]});
            var Q26;
            {var subQ0=sQuery(id+"F0.wireOp",EDGE,"E0.top");Q26=makeQuery(id+"F20.boolean.opBoolean","SPLIT",EDGE,{"disambiguationData":[TD([makeQuery(id+"F20.opExtrude","SWEPT_FACE",FACE,{"disambiguationData":[OSD([sQuery(id+"F19.wireOp",EDGE,"E90")])]})])],"derivedFrom":makeQuery(id+"F1.opExtrude","CAP_EDGE",EDGE,{"disambiguationData":[OSD([subQ0])],"isStart":true})});}
            var Q27;
            {var subQ0=sQuery(id+"F0.wireOp",EDGE,"E0.top");Q27=makeQuery(id+"F20.boolean.opBoolean","SPLIT",EDGE,{"disambiguationData":[TD([makeQuery(id+"F20.opExtrude","SWEPT_FACE",FACE,{"disambiguationData":[OSD([sQuery(id+"F19.wireOp",EDGE,"E111")])]})])],"derivedFrom":makeQuery(id+"F1.opExtrude","CAP_EDGE",EDGE,{"disambiguationData":[OSD([subQ0])],"isStart":true})});}
            var Q28;
            {var subQ0=sQuery(id+"F0.wireOp",EDGE,"E0.top");Q28=makeQuery(id+"F20.boolean.opBoolean","SPLIT",EDGE,{"disambiguationData":[TD([makeQuery(id+"F20.opExtrude","SWEPT_FACE",FACE,{"disambiguationData":[OSD([sQuery(id+"F19.wireOp",EDGE,"E108")])]})])],"derivedFrom":makeQuery(id+"F1.opExtrude","CAP_EDGE",EDGE,{"disambiguationData":[OSD([subQ0])],"isStart":true})});}
            var Q29;
            {var subQ0=sQuery(id+"F0.wireOp",EDGE,"E0.top");Q29=makeQuery(id+"F20.boolean.opBoolean","SPLIT",EDGE,{"disambiguationData":[TD([makeQuery(id+"F20.opExtrude","SWEPT_FACE",FACE,{"disambiguationData":[OSD([sQuery(id+"F19.wireOp",EDGE,"E79")])]})])],"derivedFrom":makeQuery(id+"F1.opExtrude","CAP_EDGE",EDGE,{"disambiguationData":[OSD([subQ0])],"isStart":true})});}
            var Q30;
            Q30=makeQuery(id+"F1.opExtrude","SWEPT_EDGE",EDGE,{"disambiguationData":[OSD([sQuery(id+"F0.wireOp",EDGE,"E0.top"),sQuery(id+"F0.wireOp",EDGE,"E0.left")])]});
            var Q31;
            Q31=makeQuery(id+"F1.opExtrude","CAP_EDGE",EDGE,{"disambiguationData":[OSD([sQuery(id+"F0.wireOp",EDGE,"E0.left")])],"isStart":true});
            var Q32;
            Q32=makeQuery(id+"F26.boolean.opBoolean","COPY",EDGE,{"derivedFrom":makeQuery(id+"F26.opExtrude","CAP_EDGE",EDGE,{"disambiguationData":[OSD([sQuery(id+"F25.wireOp",EDGE,"E173.left")])],"isStart":true})});
            var Q33;
            Q33=makeQuery(id+"F26.boolean.opBoolean","COPY",EDGE,{"derivedFrom":makeQuery(id+"F26.opExtrude","CAP_EDGE",EDGE,{"disambiguationData":[OSD([sQuery(id+"F25.wireOp",EDGE,"E173.right")])],"isStart":true})});
            var Q34;
            Q34=makeQuery(id+"F26.boolean.opBoolean","COPY",EDGE,{"derivedFrom":makeQuery(id+"F26.opExtrude","CAP_EDGE",EDGE,{"disambiguationData":[OSD([sQuery(id+"F25.wireOp",EDGE,"E173.bottom")])],"isStart":true})});
            var Q35;
            Q35=makeQuery(id+"F26.boolean.opBoolean","COPY",EDGE,{"derivedFrom":makeQuery(id+"F26.opExtrude","CAP_EDGE",EDGE,{"disambiguationData":[OSD([sQuery(id+"F25.wireOp",EDGE,"E173.top")])],"isStart":true})});
            var Q36;
            Q36=makeQuery(id+"F26.boolean.opBoolean","COPY",EDGE,{"derivedFrom":makeQuery(id+"F26.opExtrude","SWEPT_EDGE",EDGE,{"disambiguationData":[OSD([sQuery(id+"F25.wireOp",EDGE,"E173.top"),sQuery(id+"F25.wireOp",EDGE,"E173.left")])]})});
            var Q37;
            Q37=makeQuery(id+"F26.boolean.opBoolean","COPY",EDGE,{"derivedFrom":makeQuery(id+"F26.opExtrude","SWEPT_EDGE",EDGE,{"disambiguationData":[OSD([sQuery(id+"F25.wireOp",EDGE,"E173.top"),sQuery(id+"F25.wireOp",EDGE,"E173.right")])]})});
            var Q38;
            Q38=makeQuery(id+"F26.boolean.opBoolean","COPY",EDGE,{"derivedFrom":makeQuery(id+"F26.opExtrude","SWEPT_EDGE",EDGE,{"disambiguationData":[OSD([sQuery(id+"F25.wireOp",EDGE,"E173.bottom"),sQuery(id+"F25.wireOp",EDGE,"E173.right")])]})});
            var Q39;
            Q39=makeQuery(id+"F26.boolean.opBoolean","COPY",EDGE,{"derivedFrom":makeQuery(id+"F26.opExtrude","SWEPT_EDGE",EDGE,{"disambiguationData":[OSD([sQuery(id+"F25.wireOp",EDGE,"E173.bottom"),sQuery(id+"F25.wireOp",EDGE,"E173.left")])]})});
            fillet(context, id + "F27", {"entities" : qUnion([Q0, Q1, Q2, Q3, Q4, Q5, Q6, Q7, Q8, Q9, Q10, Q11, Q12, Q13, Q14, Q15, Q16, Q17, Q18, Q19, Q20, Q21, Q22, Q23, Q24, Q25, Q26, Q27, Q28, Q29, Q30, Q31, Q32, Q33, Q34, Q35, Q36, Q37, Q38, Q39]), "radius" : 1 * mm, "tangentPropagation" : true, "allowEdgeOverflow" : false});
        }
    });
